# Revit family: CADS_AIRFLOWdev_AirflexPro_Round_CombiDistributionBox
name_source: partatom
category: Duct Accessories
revit_build: Autodesk Revit 2015 (Build: 20160512_1515(x64)
units: mm (PartAtom-declared; Revit-internal decimal feet)

## types (2) — shared parameters
6MonthlyMaintenance = Visually inspect system, clean the fan and ducting if necessary
AirflowRateRange = 54.0 L/s
AssemblyPlace = UNKNOWN
AssetType = FIXED
B1Q = 89 mm
Body = CADS_AIRFLOWdev_SteelGalvanized
CEApproval = Yes
Clearance = 300 mm  [stored 0.984252 ft]
Color = Silver
Conn_IDia = 125 mm  [stored 0.410105 ft]
DurationUnit = Year
ExpectedServiceLife = 10
ExtPos = 176 mm
Finish = Lacquer
FireControlPanelLinks = No
Fitting Type = Ignore
FlowReturn = 0.0 L/s
Grade = Stainless
GrossWeight = 7.30 kg
Halfb1 = 178 mm
ISO140001 = Yes
ISO90001 = Yes
IsExtendedWarranty = No
LongitudinalSeam = None
Manufacturer = Airflow Developments Ltd
ManufacturerAddress = Aidelle House
Lancaster Road
Cressex Business Park
High Wycombe
Bucks
HP123QP
ManufacturerTelephone = 01494 525252
ManufacturerWebsite = www.airflow.com
Material = Steel
NBSCode = 45-80-50/394 Ventilation ducts
NominalHeight = 206 mm  [stored 0.675853 ft]
NominalLength = 500 mm  [stored 1.64042 ft]
NominalWidth = 355 mm
PassiveHouseApproval = No
PointOfContact = Airflow Developments Ltd
ProductLiterature = https://www.airflow.com
ProductionYear = 2017
Quantity = 1
RedDotDesignAward = No
ReplacementCost = 562.44
SAPApproval = Yes
ServiceLifeDuration = 10
ServiceLifeType = EXPECTEDSERVICELIFE
Shape = Rectangular
ShippingWeight = 8.76 kg
Size = 500 x 355 x 206
Status = New
TemperatureRange = up to 40°C
Uniclass2015 = Pr_30_59_96_92:Ventilation ducts
WarrantyGuarantor = Airflow Developments Ltd
WarrantyPeriod = 0
WorkingPressure = 3000.0 Pa
b1 = 355 mm
h1 = 206 mm  [stored 0.675853 ft]
l1 = 500 mm  [stored 1.64042 ft]
zero-valued in all types: CADS_Index

## per-type parameters (varying)
| type | CLOffset | Constituents | Features | LeftHand | SPRLen | SideAngle |
| Left Hand | 266 mm | 6-Spigot Combi Distribution Box (L/H) | 6-Spigot Combi Distribution Box (L/H) | Yes | 355 mm | 0.00° |
| Right Hand | 89 mm | 6-Spigot Combi Distribution Box (R/H) | 6-Spigot Combi Distribution Box (R/H) | No | 178 mm | 180.00° |

note: [stored X ft] marks values corroborated as IEEE doubles in the binary element streams (Revit-internal decimal feet)

## geometry (parser evidence)
native form markers: Blend x12, Sweep x15
no freeform markers — native parametric forms only
